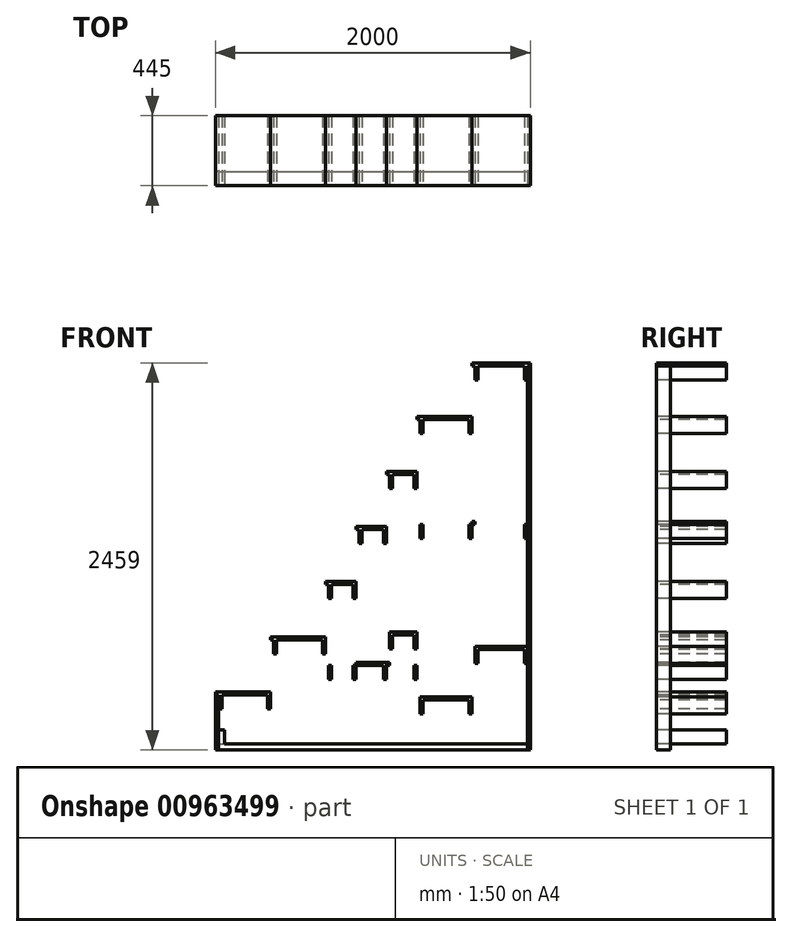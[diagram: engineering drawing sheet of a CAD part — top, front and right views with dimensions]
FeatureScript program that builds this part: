
annotation { "Feature Type Name" : "Feature", "Feature Type Description" : "" }
export const myFeature = defineFeature(function(context is Context, id is Id, definition is map)
    precondition{}
    {
        {
            var Q0;
            Q0=qCreatedBy(makeId("Front.planeOp"),FACE);
            var sketch = newSketch(context, id + "F0", { "sketchPlane" : qUnion([Q0])});
            skLineSegment(sketch, "E0.bottom", {"start": v(0, 0) * mm, "end": v(1962, 0) * mm});
            skLineSegment(sketch, "E0.top", {"start": v(0, 38) * mm, "end": v(1962, 38) * mm});
            skLineSegment(sketch, "E0.left", {"start": v(0, 0) * mm, "end": v(0, 38) * mm});
            skLineSegment(sketch, "E0.right", {"start": v(1962, 0) * mm, "end": v(1962, 38) * mm});
            skLineSegment(sketch, "E1.bottom", {"start": v(0, 0) * mm, "end": v(-19, 0) * mm});
            skLineSegment(sketch, "E1.top", {"start": v(0, 350) * mm, "end": v(-19, 350) * mm});
            skLineSegment(sketch, "E1.left", {"start": v(0, 0) * mm, "end": v(0, 350) * mm});
            skLineSegment(sketch, "E1.right", {"start": v(-19, 0) * mm, "end": v(-19, 350) * mm});
            skLineSegment(sketch, "E2.bottom", {"start": v(1962, 0) * mm, "end": v(1981, 0) * mm});
            skLineSegment(sketch, "E2.top", {"start": v(1962, 2440) * mm, "end": v(1981, 2440) * mm});
            skLineSegment(sketch, "E2.left", {"start": v(1962, 0) * mm, "end": v(1962, 2440) * mm});
            skLineSegment(sketch, "E2.right", {"start": v(1981, 0) * mm, "end": v(1981, 2440) * mm});
            skLineSegment(sketch, "E3.bottom", {"start": v(331, 38) * mm, "end": v(350, 38) * mm});
            skLineSegment(sketch, "E3.top", {"start": v(331, 700) * mm, "end": v(350, 700) * mm});
            skLineSegment(sketch, "E3.left", {"start": v(331, 38) * mm, "end": v(331, 700) * mm});
            skLineSegment(sketch, "E3.right", {"start": v(350, 38) * mm, "end": v(350, 700) * mm});
            skLineSegment(sketch, "E4.bottom", {"start": v(681, 38) * mm, "end": v(700, 38) * mm});
            skLineSegment(sketch, "E4.top", {"start": v(681, 1050) * mm, "end": v(700, 1050) * mm});
            skLineSegment(sketch, "E4.left", {"start": v(681, 38) * mm, "end": v(681, 1050) * mm});
            skLineSegment(sketch, "E4.right", {"start": v(700, 38) * mm, "end": v(700, 1050) * mm});
            skLineSegment(sketch, "E5.bottom", {"start": v(874.67, 38) * mm, "end": v(893.67, 38) * mm});
            skLineSegment(sketch, "E5.top", {"start": v(874.67, 1400) * mm, "end": v(893.67, 1400) * mm});
            skLineSegment(sketch, "E5.left", {"start": v(874.67, 38) * mm, "end": v(874.67, 1400) * mm});
            skLineSegment(sketch, "E5.right", {"start": v(893.67, 38) * mm, "end": v(893.67, 1400) * mm});
            skLineSegment(sketch, "E6.bottom", {"start": v(1068.34, 38) * mm, "end": v(1087.34, 38) * mm});
            skLineSegment(sketch, "E6.top", {"start": v(1068.34, 1750) * mm, "end": v(1087.34, 1750) * mm});
            skLineSegment(sketch, "E6.left", {"start": v(1068.34, 38) * mm, "end": v(1068.34, 1750) * mm});
            skLineSegment(sketch, "E6.right", {"start": v(1087.34, 38) * mm, "end": v(1087.34, 1750) * mm});
            skLineSegment(sketch, "E7.bottom", {"start": v(1262, 38) * mm, "end": v(1281, 38) * mm});
            skLineSegment(sketch, "E7.top", {"start": v(1262, 2100) * mm, "end": v(1281, 2100) * mm});
            skLineSegment(sketch, "E7.left", {"start": v(1262, 38) * mm, "end": v(1262, 2100) * mm});
            skLineSegment(sketch, "E7.right", {"start": v(1281, 38) * mm, "end": v(1281, 2100) * mm});
            skLineSegment(sketch, "E8.bottom", {"start": v(1612, 38) * mm, "end": v(1631, 38) * mm});
            skLineSegment(sketch, "E8.top", {"start": v(1612, 2440) * mm, "end": v(1631, 2440) * mm});
            skLineSegment(sketch, "E8.left", {"start": v(1612, 38) * mm, "end": v(1612, 2440) * mm});
            skLineSegment(sketch, "E8.right", {"start": v(1631, 38) * mm, "end": v(1631, 2440) * mm});
            skLineSegment(sketch, "E9", {"start": v(1612, 2440) * mm, "end": v(1962, 2440) * mm});
            skLineSegment(sketch, "E10", {"start": v(1281, 2100) * mm, "end": v(1612, 2100) * mm});
            skLineSegment(sketch, "E11", {"start": v(1087.34, 1750) * mm, "end": v(1262, 1750) * mm});
            skLineSegment(sketch, "E12", {"start": v(893.67, 1400) * mm, "end": v(1068.34, 1400) * mm});
            skLineSegment(sketch, "E13", {"start": v(700, 1050) * mm, "end": v(874.67, 1050) * mm});
            skLineSegment(sketch, "E14", {"start": v(350, 700) * mm, "end": v(681, 700) * mm});
            skLineSegment(sketch, "E15", {"start": v(0, 350) * mm, "end": v(331, 350) * mm});
            skLineSegment(sketch, "E16.bottom", {"start": v(0, 127) * mm, "end": v(38, 127) * mm});
            skLineSegment(sketch, "E16.top", {"start": v(0, 38) * mm, "end": v(38, 38) * mm});
            skLineSegment(sketch, "E16.left", {"start": v(0, 127) * mm, "end": v(0, 38) * mm});
            skLineSegment(sketch, "E16.right", {"start": v(38, 127) * mm, "end": v(38, 38) * mm});
            skLineSegment(sketch, "E17.bottom", {"start": v(0, 350) * mm, "end": v(22.52, 350) * mm});
            skLineSegment(sketch, "E17.top", {"start": v(0, 261) * mm, "end": v(22.52, 261) * mm});
            skLineSegment(sketch, "E17.left", {"start": v(0, 350) * mm, "end": v(0, 261) * mm});
            skLineSegment(sketch, "E17.right", {"start": v(22.52, 350) * mm, "end": v(22.52, 261) * mm});
            skLineSegment(sketch, "E18.bottom", {"start": v(312, 350) * mm, "end": v(331, 350) * mm});
            skLineSegment(sketch, "E18.top", {"start": v(312, 261) * mm, "end": v(331, 261) * mm});
            skLineSegment(sketch, "E18.left", {"start": v(312, 350) * mm, "end": v(312, 261) * mm});
            skLineSegment(sketch, "E18.right", {"start": v(331, 350) * mm, "end": v(331, 261) * mm});
            skLineSegment(sketch, "E19.bottom", {"start": v(-19, 350) * mm, "end": v(331, 350) * mm});
            skLineSegment(sketch, "E19.top", {"start": v(-19, 369) * mm, "end": v(331, 369) * mm});
            skLineSegment(sketch, "E19.left", {"start": v(-19, 350) * mm, "end": v(-19, 369) * mm});
            skLineSegment(sketch, "E19.right", {"start": v(331, 350) * mm, "end": v(331, 369) * mm});
            skLineSegment(sketch, "E20.bottom", {"start": v(350, 700) * mm, "end": v(369, 700) * mm});
            skLineSegment(sketch, "E20.top", {"start": v(350, 611) * mm, "end": v(369, 611) * mm});
            skLineSegment(sketch, "E20.left", {"start": v(350, 700) * mm, "end": v(350, 611) * mm});
            skLineSegment(sketch, "E20.right", {"start": v(369, 700) * mm, "end": v(369, 611) * mm});
            skLineSegment(sketch, "E21.bottom", {"start": v(681, 700) * mm, "end": v(662, 700) * mm});
            skLineSegment(sketch, "E21.top", {"start": v(681, 611) * mm, "end": v(662, 611) * mm});
            skLineSegment(sketch, "E21.left", {"start": v(681, 700) * mm, "end": v(681, 611) * mm});
            skLineSegment(sketch, "E21.right", {"start": v(662, 700) * mm, "end": v(662, 611) * mm});
            skLineSegment(sketch, "E22.bottom", {"start": v(331, 700) * mm, "end": v(681, 700) * mm});
            skLineSegment(sketch, "E22.top", {"start": v(331, 719) * mm, "end": v(681, 719) * mm});
            skLineSegment(sketch, "E22.left", {"start": v(331, 700) * mm, "end": v(331, 719) * mm});
            skLineSegment(sketch, "E22.right", {"start": v(681, 700) * mm, "end": v(681, 719) * mm});
            skLineSegment(sketch, "E23.bottom", {"start": v(700, 1050) * mm, "end": v(719, 1050) * mm});
            skLineSegment(sketch, "E23.top", {"start": v(700, 961) * mm, "end": v(719, 961) * mm});
            skLineSegment(sketch, "E23.left", {"start": v(700, 1050) * mm, "end": v(700, 961) * mm});
            skLineSegment(sketch, "E23.right", {"start": v(719, 1050) * mm, "end": v(719, 961) * mm});
            skLineSegment(sketch, "E24.bottom", {"start": v(874.67, 1050) * mm, "end": v(855.67, 1050) * mm});
            skLineSegment(sketch, "E24.top", {"start": v(874.67, 961) * mm, "end": v(855.67, 961) * mm});
            skLineSegment(sketch, "E24.left", {"start": v(874.67, 1050) * mm, "end": v(874.67, 961) * mm});
            skLineSegment(sketch, "E24.right", {"start": v(855.67, 1050) * mm, "end": v(855.67, 961) * mm});
            skLineSegment(sketch, "E25.bottom", {"start": v(681, 1050) * mm, "end": v(874.67, 1050) * mm});
            skLineSegment(sketch, "E25.top", {"start": v(681, 1069) * mm, "end": v(874.67, 1069) * mm});
            skLineSegment(sketch, "E25.left", {"start": v(681, 1050) * mm, "end": v(681, 1069) * mm});
            skLineSegment(sketch, "E25.right", {"start": v(874.67, 1050) * mm, "end": v(874.67, 1069) * mm});
            skLineSegment(sketch, "E26.bottom", {"start": v(893.67, 1400) * mm, "end": v(912.67, 1400) * mm});
            skLineSegment(sketch, "E26.top", {"start": v(893.67, 1311) * mm, "end": v(912.67, 1311) * mm});
            skLineSegment(sketch, "E26.left", {"start": v(893.67, 1400) * mm, "end": v(893.67, 1311) * mm});
            skLineSegment(sketch, "E26.right", {"start": v(912.67, 1400) * mm, "end": v(912.67, 1311) * mm});
            skLineSegment(sketch, "E27.bottom", {"start": v(1068.34, 1400) * mm, "end": v(1049.34, 1400) * mm});
            skLineSegment(sketch, "E27.top", {"start": v(1068.34, 1311) * mm, "end": v(1049.34, 1311) * mm});
            skLineSegment(sketch, "E27.left", {"start": v(1068.34, 1400) * mm, "end": v(1068.34, 1311) * mm});
            skLineSegment(sketch, "E27.right", {"start": v(1049.34, 1400) * mm, "end": v(1049.34, 1311) * mm});
            skLineSegment(sketch, "E28.bottom", {"start": v(874.67, 1400) * mm, "end": v(1068.34, 1400) * mm});
            skLineSegment(sketch, "E28.top", {"start": v(874.67, 1419) * mm, "end": v(1068.34, 1419) * mm});
            skLineSegment(sketch, "E28.left", {"start": v(874.67, 1400) * mm, "end": v(874.67, 1419) * mm});
            skLineSegment(sketch, "E28.right", {"start": v(1068.34, 1400) * mm, "end": v(1068.34, 1419) * mm});
            skLineSegment(sketch, "E29.bottom", {"start": v(1087.34, 1750) * mm, "end": v(1106.34, 1750) * mm});
            skLineSegment(sketch, "E29.top", {"start": v(1087.34, 1661) * mm, "end": v(1106.34, 1661) * mm});
            skLineSegment(sketch, "E29.left", {"start": v(1087.34, 1750) * mm, "end": v(1087.34, 1661) * mm});
            skLineSegment(sketch, "E29.right", {"start": v(1106.34, 1750) * mm, "end": v(1106.34, 1661) * mm});
            skLineSegment(sketch, "E30.bottom", {"start": v(1262, 1750) * mm, "end": v(1243, 1750) * mm});
            skLineSegment(sketch, "E30.top", {"start": v(1262, 1661) * mm, "end": v(1243, 1661) * mm});
            skLineSegment(sketch, "E30.left", {"start": v(1262, 1750) * mm, "end": v(1262, 1661) * mm});
            skLineSegment(sketch, "E30.right", {"start": v(1243, 1750) * mm, "end": v(1243, 1661) * mm});
            skLineSegment(sketch, "E31.bottom", {"start": v(1281, 2100) * mm, "end": v(1300, 2100) * mm});
            skLineSegment(sketch, "E31.top", {"start": v(1281, 2011) * mm, "end": v(1300, 2011) * mm});
            skLineSegment(sketch, "E31.left", {"start": v(1281, 2100) * mm, "end": v(1281, 2011) * mm});
            skLineSegment(sketch, "E31.right", {"start": v(1300, 2100) * mm, "end": v(1300, 2011) * mm});
            skLineSegment(sketch, "E32.bottom", {"start": v(1612, 2100) * mm, "end": v(1593, 2100) * mm});
            skLineSegment(sketch, "E32.top", {"start": v(1612, 2011) * mm, "end": v(1593, 2011) * mm});
            skLineSegment(sketch, "E32.left", {"start": v(1612, 2100) * mm, "end": v(1612, 2011) * mm});
            skLineSegment(sketch, "E32.right", {"start": v(1593, 2100) * mm, "end": v(1593, 2011) * mm});
            skLineSegment(sketch, "E33.bottom", {"start": v(1068.34, 1750) * mm, "end": v(1262, 1750) * mm});
            skLineSegment(sketch, "E33.top", {"start": v(1068.34, 1769) * mm, "end": v(1262, 1769) * mm});
            skLineSegment(sketch, "E33.left", {"start": v(1068.34, 1750) * mm, "end": v(1068.34, 1769) * mm});
            skLineSegment(sketch, "E33.right", {"start": v(1262, 1750) * mm, "end": v(1262, 1769) * mm});
            skLineSegment(sketch, "E34.bottom", {"start": v(1262, 2100) * mm, "end": v(1612, 2100) * mm});
            skLineSegment(sketch, "E34.top", {"start": v(1262, 2119) * mm, "end": v(1612, 2119) * mm});
            skLineSegment(sketch, "E34.left", {"start": v(1262, 2100) * mm, "end": v(1262, 2119) * mm});
            skLineSegment(sketch, "E34.right", {"start": v(1612, 2100) * mm, "end": v(1612, 2119) * mm});
            skLineSegment(sketch, "E35.bottom", {"start": v(1631, 2440) * mm, "end": v(1650, 2440) * mm});
            skLineSegment(sketch, "E35.top", {"start": v(1631, 2351) * mm, "end": v(1650, 2351) * mm});
            skLineSegment(sketch, "E35.left", {"start": v(1631, 2440) * mm, "end": v(1631, 2351) * mm});
            skLineSegment(sketch, "E35.right", {"start": v(1650, 2440) * mm, "end": v(1650, 2351) * mm});
            skLineSegment(sketch, "E36.bottom", {"start": v(1962, 2440) * mm, "end": v(1943, 2440) * mm});
            skLineSegment(sketch, "E36.top", {"start": v(1962, 2351) * mm, "end": v(1943, 2351) * mm});
            skLineSegment(sketch, "E36.left", {"start": v(1962, 2440) * mm, "end": v(1962, 2351) * mm});
            skLineSegment(sketch, "E36.right", {"start": v(1943, 2440) * mm, "end": v(1943, 2351) * mm});
            skLineSegment(sketch, "E37.bottom", {"start": v(1612, 2440) * mm, "end": v(1981, 2440) * mm});
            skLineSegment(sketch, "E37.top", {"start": v(1612, 2459) * mm, "end": v(1981, 2459) * mm});
            skLineSegment(sketch, "E37.left", {"start": v(1612, 2440) * mm, "end": v(1612, 2459) * mm});
            skLineSegment(sketch, "E37.right", {"start": v(1981, 2440) * mm, "end": v(1981, 2459) * mm});
            skLineSegment(sketch, "E38", {"start": v(1631, 638) * mm, "end": v(1962, 638) * mm});
            skLineSegment(sketch, "E39", {"start": v(1281, 319) * mm, "end": v(1612, 319) * mm});
            skLineSegment(sketch, "E40", {"start": v(1087.34, 731.7) * mm, "end": v(1262, 731.7) * mm});
            skLineSegment(sketch, "E41", {"start": v(1281, 1431.7) * mm, "end": v(1962, 1431.7) * mm});
            skLineSegment(sketch, "E42.bottom", {"start": v(1631, 638) * mm, "end": v(1650, 638) * mm});
            skLineSegment(sketch, "E42.top", {"start": v(1631, 549) * mm, "end": v(1650, 549) * mm});
            skLineSegment(sketch, "E42.left", {"start": v(1631, 638) * mm, "end": v(1631, 549) * mm});
            skLineSegment(sketch, "E42.right", {"start": v(1650, 638) * mm, "end": v(1650, 549) * mm});
            skLineSegment(sketch, "E43.bottom", {"start": v(1962, 638) * mm, "end": v(1943, 638) * mm});
            skLineSegment(sketch, "E43.top", {"start": v(1962, 549) * mm, "end": v(1943, 549) * mm});
            skLineSegment(sketch, "E43.left", {"start": v(1962, 638) * mm, "end": v(1962, 549) * mm});
            skLineSegment(sketch, "E43.right", {"start": v(1943, 638) * mm, "end": v(1943, 549) * mm});
            skLineSegment(sketch, "E44.bottom", {"start": v(1281, 319) * mm, "end": v(1300, 319) * mm});
            skLineSegment(sketch, "E44.top", {"start": v(1281, 230) * mm, "end": v(1300, 230) * mm});
            skLineSegment(sketch, "E44.left", {"start": v(1281, 319) * mm, "end": v(1281, 230) * mm});
            skLineSegment(sketch, "E44.right", {"start": v(1300, 319) * mm, "end": v(1300, 230) * mm});
            skLineSegment(sketch, "E45.bottom", {"start": v(1612, 319) * mm, "end": v(1593, 319) * mm});
            skLineSegment(sketch, "E45.top", {"start": v(1612, 230) * mm, "end": v(1593, 230) * mm});
            skLineSegment(sketch, "E45.left", {"start": v(1612, 319) * mm, "end": v(1612, 230) * mm});
            skLineSegment(sketch, "E45.right", {"start": v(1593, 319) * mm, "end": v(1593, 230) * mm});
            skLineSegment(sketch, "E46.bottom", {"start": v(1087.34, 731.7) * mm, "end": v(1106.34, 731.7) * mm});
            skLineSegment(sketch, "E46.top", {"start": v(1087.34, 642.7) * mm, "end": v(1106.34, 642.7) * mm});
            skLineSegment(sketch, "E46.left", {"start": v(1087.34, 731.7) * mm, "end": v(1087.34, 642.7) * mm});
            skLineSegment(sketch, "E46.right", {"start": v(1106.34, 731.7) * mm, "end": v(1106.34, 642.7) * mm});
            skLineSegment(sketch, "E47.bottom", {"start": v(1262, 731.7) * mm, "end": v(1243, 731.7) * mm});
            skLineSegment(sketch, "E47.top", {"start": v(1262, 642.7) * mm, "end": v(1243, 642.7) * mm});
            skLineSegment(sketch, "E47.left", {"start": v(1262, 731.7) * mm, "end": v(1262, 642.7) * mm});
            skLineSegment(sketch, "E47.right", {"start": v(1243, 731.7) * mm, "end": v(1243, 642.7) * mm});
            skLineSegment(sketch, "E48.bottom", {"start": v(1281, 1431.7) * mm, "end": v(1300, 1431.7) * mm});
            skLineSegment(sketch, "E48.top", {"start": v(1281, 1342.7) * mm, "end": v(1300, 1342.7) * mm});
            skLineSegment(sketch, "E48.left", {"start": v(1281, 1431.7) * mm, "end": v(1281, 1342.7) * mm});
            skLineSegment(sketch, "E48.right", {"start": v(1300, 1431.7) * mm, "end": v(1300, 1342.7) * mm});
            skLineSegment(sketch, "E49.bottom", {"start": v(1612, 1431.7) * mm, "end": v(1593, 1431.7) * mm});
            skLineSegment(sketch, "E49.top", {"start": v(1612, 1342.7) * mm, "end": v(1593, 1342.7) * mm});
            skLineSegment(sketch, "E49.left", {"start": v(1612, 1431.7) * mm, "end": v(1612, 1342.7) * mm});
            skLineSegment(sketch, "E49.right", {"start": v(1593, 1431.7) * mm, "end": v(1593, 1342.7) * mm});
            skLineSegment(sketch, "E50.bottom", {"start": v(1962, 1431.7) * mm, "end": v(1943, 1431.7) * mm});
            skLineSegment(sketch, "E50.top", {"start": v(1962, 1342.7) * mm, "end": v(1943, 1342.7) * mm});
            skLineSegment(sketch, "E50.left", {"start": v(1962, 1431.7) * mm, "end": v(1962, 1342.7) * mm});
            skLineSegment(sketch, "E50.right", {"start": v(1943, 1431.7) * mm, "end": v(1943, 1342.7) * mm});
            skLineSegment(sketch, "E51.top", {"start": v(1631, 657) * mm, "end": v(1962, 657) * mm});
            skLineSegment(sketch, "E51.left", {"start": v(1631, 638) * mm, "end": v(1631, 657) * mm});
            skLineSegment(sketch, "E51.right", {"start": v(1962, 638) * mm, "end": v(1962, 657) * mm});
            skLineSegment(sketch, "E52.top", {"start": v(1281, 338) * mm, "end": v(1612, 338) * mm});
            skLineSegment(sketch, "E52.left", {"start": v(1281, 319) * mm, "end": v(1281, 338) * mm});
            skLineSegment(sketch, "E52.right", {"start": v(1612, 319) * mm, "end": v(1612, 338) * mm});
            skLineSegment(sketch, "E53.top", {"start": v(1087.34, 750.7) * mm, "end": v(1262, 750.7) * mm});
            skLineSegment(sketch, "E53.left", {"start": v(1087.34, 731.7) * mm, "end": v(1087.34, 750.7) * mm});
            skLineSegment(sketch, "E53.right", {"start": v(1262, 731.7) * mm, "end": v(1262, 750.7) * mm});
            skLineSegment(sketch, "E54.top", {"start": v(1281, 1450.7) * mm, "end": v(1962, 1450.7) * mm});
            skLineSegment(sketch, "E54.left", {"start": v(1281, 1431.7) * mm, "end": v(1281, 1450.7) * mm});
            skLineSegment(sketch, "E54.right", {"start": v(1962, 1431.7) * mm, "end": v(1962, 1450.7) * mm});
            skLineSegment(sketch, "E55.bottom", {"start": v(700, 538) * mm, "end": v(719, 538) * mm});
            skLineSegment(sketch, "E55.top", {"start": v(700, 449) * mm, "end": v(719, 449) * mm});
            skLineSegment(sketch, "E55.left", {"start": v(700, 538) * mm, "end": v(700, 449) * mm});
            skLineSegment(sketch, "E55.right", {"start": v(719, 538) * mm, "end": v(719, 449) * mm});
            skLineSegment(sketch, "E56.bottom", {"start": v(874.3, 538) * mm, "end": v(855.3, 538) * mm});
            skLineSegment(sketch, "E56.top", {"start": v(874.3, 449) * mm, "end": v(855.3, 449) * mm});
            skLineSegment(sketch, "E56.left", {"start": v(874.3, 538) * mm, "end": v(874.3, 449) * mm});
            skLineSegment(sketch, "E56.right", {"start": v(855.3, 538) * mm, "end": v(855.3, 449) * mm});
            skLineSegment(sketch, "E57.bottom", {"start": v(1068.34, 538) * mm, "end": v(1049.34, 538) * mm});
            skLineSegment(sketch, "E57.top", {"start": v(1068.34, 449) * mm, "end": v(1049.34, 449) * mm});
            skLineSegment(sketch, "E57.left", {"start": v(1068.34, 538) * mm, "end": v(1068.34, 449) * mm});
            skLineSegment(sketch, "E57.right", {"start": v(1049.34, 538) * mm, "end": v(1049.34, 449) * mm});
            skLineSegment(sketch, "E58.bottom", {"start": v(1262, 538) * mm, "end": v(1243, 538) * mm});
            skLineSegment(sketch, "E58.top", {"start": v(1262, 449) * mm, "end": v(1243, 449) * mm});
            skLineSegment(sketch, "E58.left", {"start": v(1262, 538) * mm, "end": v(1262, 449) * mm});
            skLineSegment(sketch, "E58.right", {"start": v(1243, 538) * mm, "end": v(1243, 449) * mm});
            skLineSegment(sketch, "E59.bottom", {"start": v(700, 538) * mm, "end": v(1262, 538) * mm});
            skLineSegment(sketch, "E59.top", {"start": v(700, 557) * mm, "end": v(1262, 557) * mm});
            skLineSegment(sketch, "E59.left", {"start": v(700, 538) * mm, "end": v(700, 557) * mm});
            skLineSegment(sketch, "E59.right", {"start": v(1262, 538) * mm, "end": v(1262, 557) * mm});
            skLineSegment(sketch, "E60.bottom", {"start": v(350, 38) * mm, "end": v(388, 38) * mm});
            skLineSegment(sketch, "E60.top", {"start": v(350, 127) * mm, "end": v(388, 127) * mm});
            skLineSegment(sketch, "E60.left", {"start": v(350, 38) * mm, "end": v(350, 127) * mm});
            skLineSegment(sketch, "E60.right", {"start": v(388, 38) * mm, "end": v(388, 127) * mm});
            skLineSegment(sketch, "E61.bottom", {"start": v(700, 38) * mm, "end": v(738, 38) * mm});
            skLineSegment(sketch, "E61.top", {"start": v(700, 127) * mm, "end": v(738, 127) * mm});
            skLineSegment(sketch, "E61.left", {"start": v(700, 38) * mm, "end": v(700, 127) * mm});
            skLineSegment(sketch, "E61.right", {"start": v(738, 38) * mm, "end": v(738, 127) * mm});
            skLineSegment(sketch, "E62.bottom", {"start": v(893.67, 38) * mm, "end": v(931.67, 38) * mm});
            skLineSegment(sketch, "E62.top", {"start": v(893.67, 127) * mm, "end": v(931.67, 127) * mm});
            skLineSegment(sketch, "E62.left", {"start": v(893.67, 38) * mm, "end": v(893.67, 127) * mm});
            skLineSegment(sketch, "E62.right", {"start": v(931.67, 38) * mm, "end": v(931.67, 127) * mm});
            skLineSegment(sketch, "E63.bottom", {"start": v(1087.34, 38) * mm, "end": v(1125.34, 38) * mm});
            skLineSegment(sketch, "E63.top", {"start": v(1087.34, 127) * mm, "end": v(1125.34, 127) * mm});
            skLineSegment(sketch, "E63.left", {"start": v(1087.34, 38) * mm, "end": v(1087.34, 127) * mm});
            skLineSegment(sketch, "E63.right", {"start": v(1125.34, 38) * mm, "end": v(1125.34, 127) * mm});
            skLineSegment(sketch, "E64.bottom", {"start": v(1281, 38) * mm, "end": v(1319, 38) * mm});
            skLineSegment(sketch, "E64.top", {"start": v(1281, 127) * mm, "end": v(1319, 127) * mm});
            skLineSegment(sketch, "E64.left", {"start": v(1281, 38) * mm, "end": v(1281, 127) * mm});
            skLineSegment(sketch, "E64.right", {"start": v(1319, 38) * mm, "end": v(1319, 127) * mm});
            skLineSegment(sketch, "E65.bottom", {"start": v(1631, 38) * mm, "end": v(1669, 38) * mm});
            skLineSegment(sketch, "E65.top", {"start": v(1631, 127) * mm, "end": v(1669, 127) * mm});
            skLineSegment(sketch, "E65.left", {"start": v(1631, 38) * mm, "end": v(1631, 127) * mm});
            skLineSegment(sketch, "E65.right", {"start": v(1669, 38) * mm, "end": v(1669, 127) * mm});
            skLineSegment(sketch, "E66.bottom", {"start": v(1962, 38) * mm, "end": v(1924, 38) * mm});
            skLineSegment(sketch, "E66.top", {"start": v(1962, 127) * mm, "end": v(1924, 127) * mm});
            skLineSegment(sketch, "E66.left", {"start": v(1962, 38) * mm, "end": v(1962, 127) * mm});
            skLineSegment(sketch, "E66.right", {"start": v(1924, 38) * mm, "end": v(1924, 127) * mm});
            skSolve(sketch);
        }
        {
            var Q0;
            {var subQ12=sQuery(id+"F0.wireOp",EDGE,"E0.bottom");Q0=makeQuery(id+"F0.imprint","IMPRINT",FACE,{"disambiguationData":[TD([[makeQuery(id+"F0.imprint","IMPRINT",EDGE,{"derivedFrom":subQ12}),1.0]])]});}
            extrude(context, id + "F1", {"entities" : qUnion([Q0]), "oppositeDirection" : true, "depth" : 89 * mm, "offsetDistance" : 25 * mm});
        }
        {
            var Q0;
            Q0=makeQuery(id+"F0.imprint","IMPRINT",FACE,{"disambiguationData":[TD([[makeQuery(id+"F0.imprint","IMPRINT",EDGE,{"derivedFrom":sQuery(id+"F0.wireOp",EDGE,"E16.bottom")}),-1.0]])]});
            var Q1;
            Q1=makeQuery(id+"F0.imprint","IMPRINT",FACE,{"disambiguationData":[TD([[makeQuery(id+"F0.imprint","IMPRINT",EDGE,{"derivedFrom":sQuery(id+"F0.wireOp",EDGE,"E60.bottom")}),1.0]])]});
            var Q2;
            Q2=makeQuery(id+"F0.imprint","IMPRINT",FACE,{"disambiguationData":[TD([[makeQuery(id+"F0.imprint","IMPRINT",EDGE,{"derivedFrom":sQuery(id+"F0.wireOp",EDGE,"E61.bottom")}),1.0]])]});
            var Q3;
            Q3=makeQuery(id+"F0.imprint","IMPRINT",FACE,{"disambiguationData":[TD([[makeQuery(id+"F0.imprint","IMPRINT",EDGE,{"derivedFrom":sQuery(id+"F0.wireOp",EDGE,"E62.bottom")}),1.0]])]});
            var Q4;
            Q4=makeQuery(id+"F0.imprint","IMPRINT",FACE,{"disambiguationData":[TD([[makeQuery(id+"F0.imprint","IMPRINT",EDGE,{"derivedFrom":sQuery(id+"F0.wireOp",EDGE,"E63.bottom")}),1.0]])]});
            var Q5;
            Q5=makeQuery(id+"F0.imprint","IMPRINT",FACE,{"disambiguationData":[TD([[makeQuery(id+"F0.imprint","IMPRINT",EDGE,{"derivedFrom":sQuery(id+"F0.wireOp",EDGE,"E64.bottom")}),1.0]])]});
            var Q6;
            Q6=makeQuery(id+"F0.imprint","IMPRINT",FACE,{"disambiguationData":[TD([[makeQuery(id+"F0.imprint","IMPRINT",EDGE,{"derivedFrom":sQuery(id+"F0.wireOp",EDGE,"E65.bottom")}),1.0]])]});
            var Q7;
            Q7=makeQuery(id+"F0.imprint","IMPRINT",FACE,{"disambiguationData":[TD([[makeQuery(id+"F0.imprint","IMPRINT",EDGE,{"derivedFrom":sQuery(id+"F0.wireOp",EDGE,"E66.bottom")}),-1.0]])]});
            var Q8;
            Q8=makeQuery(id+"F0.imprint","IMPRINT",FACE,{"disambiguationData":[TD([[makeQuery(id+"F0.imprint","IMPRINT",EDGE,{"derivedFrom":sQuery(id+"F0.wireOp",EDGE,"E45.top")}),-1.0]])]});
            var Q9;
            Q9=makeQuery(id+"F0.imprint","IMPRINT",FACE,{"disambiguationData":[TD([[makeQuery(id+"F0.imprint","IMPRINT",EDGE,{"derivedFrom":sQuery(id+"F0.wireOp",EDGE,"E44.top")}),1.0]])]});
            var Q10;
            Q10=makeQuery(id+"F0.imprint","IMPRINT",FACE,{"disambiguationData":[TD([[makeQuery(id+"F0.imprint","IMPRINT",EDGE,{"derivedFrom":sQuery(id+"F0.wireOp",EDGE,"E58.top")}),-1.0]])]});
            var Q11;
            Q11=makeQuery(id+"F0.imprint","IMPRINT",FACE,{"disambiguationData":[TD([[makeQuery(id+"F0.imprint","IMPRINT",EDGE,{"derivedFrom":sQuery(id+"F0.wireOp",EDGE,"E57.top")}),-1.0]])]});
            var Q12;
            Q12=makeQuery(id+"F0.imprint","IMPRINT",FACE,{"disambiguationData":[TD([[makeQuery(id+"F0.imprint","IMPRINT",EDGE,{"derivedFrom":sQuery(id+"F0.wireOp",EDGE,"E56.top")}),-1.0]])]});
            var Q13;
            Q13=makeQuery(id+"F0.imprint","IMPRINT",FACE,{"disambiguationData":[TD([[makeQuery(id+"F0.imprint","IMPRINT",EDGE,{"derivedFrom":sQuery(id+"F0.wireOp",EDGE,"E55.top")}),1.0]])]});
            var Q14;
            Q14=makeQuery(id+"F0.imprint","IMPRINT",FACE,{"disambiguationData":[TD([[makeQuery(id+"F0.imprint","IMPRINT",EDGE,{"derivedFrom":sQuery(id+"F0.wireOp",EDGE,"E18.top")}),1.0]])]});
            var Q15;
            Q15=makeQuery(id+"F0.imprint","IMPRINT",FACE,{"disambiguationData":[TD([[makeQuery(id+"F0.imprint","IMPRINT",EDGE,{"derivedFrom":sQuery(id+"F0.wireOp",EDGE,"E17.top")}),1.0]])]});
            var Q16;
            Q16=makeQuery(id+"F0.imprint","IMPRINT",FACE,{"disambiguationData":[TD([[makeQuery(id+"F0.imprint","IMPRINT",EDGE,{"derivedFrom":sQuery(id+"F0.wireOp",EDGE,"E20.top")}),1.0]])]});
            var Q17;
            Q17=makeQuery(id+"F0.imprint","IMPRINT",FACE,{"disambiguationData":[TD([[makeQuery(id+"F0.imprint","IMPRINT",EDGE,{"derivedFrom":sQuery(id+"F0.wireOp",EDGE,"E21.top")}),-1.0]])]});
            var Q18;
            Q18=makeQuery(id+"F0.imprint","IMPRINT",FACE,{"disambiguationData":[TD([[makeQuery(id+"F0.imprint","IMPRINT",EDGE,{"derivedFrom":sQuery(id+"F0.wireOp",EDGE,"E46.top")}),1.0]])]});
            var Q19;
            Q19=makeQuery(id+"F0.imprint","IMPRINT",FACE,{"disambiguationData":[TD([[makeQuery(id+"F0.imprint","IMPRINT",EDGE,{"derivedFrom":sQuery(id+"F0.wireOp",EDGE,"E47.top")}),-1.0]])]});
            var Q20;
            Q20=makeQuery(id+"F0.imprint","IMPRINT",FACE,{"disambiguationData":[TD([[makeQuery(id+"F0.imprint","IMPRINT",EDGE,{"derivedFrom":sQuery(id+"F0.wireOp",EDGE,"E42.top")}),1.0]])]});
            var Q21;
            Q21=makeQuery(id+"F0.imprint","IMPRINT",FACE,{"disambiguationData":[TD([[makeQuery(id+"F0.imprint","IMPRINT",EDGE,{"derivedFrom":sQuery(id+"F0.wireOp",EDGE,"E43.top")}),-1.0]])]});
            var Q22;
            Q22=makeQuery(id+"F0.imprint","IMPRINT",FACE,{"disambiguationData":[TD([[makeQuery(id+"F0.imprint","IMPRINT",EDGE,{"derivedFrom":sQuery(id+"F0.wireOp",EDGE,"E23.top")}),1.0]])]});
            var Q23;
            Q23=makeQuery(id+"F0.imprint","IMPRINT",FACE,{"disambiguationData":[TD([[makeQuery(id+"F0.imprint","IMPRINT",EDGE,{"derivedFrom":sQuery(id+"F0.wireOp",EDGE,"E24.top")}),-1.0]])]});
            var Q24;
            Q24=makeQuery(id+"F0.imprint","IMPRINT",FACE,{"disambiguationData":[TD([[makeQuery(id+"F0.imprint","IMPRINT",EDGE,{"derivedFrom":sQuery(id+"F0.wireOp",EDGE,"E26.top")}),1.0]])]});
            var Q25;
            Q25=makeQuery(id+"F0.imprint","IMPRINT",FACE,{"disambiguationData":[TD([[makeQuery(id+"F0.imprint","IMPRINT",EDGE,{"derivedFrom":sQuery(id+"F0.wireOp",EDGE,"E27.top")}),-1.0]])]});
            var Q26;
            Q26=makeQuery(id+"F0.imprint","IMPRINT",FACE,{"disambiguationData":[TD([[makeQuery(id+"F0.imprint","IMPRINT",EDGE,{"derivedFrom":sQuery(id+"F0.wireOp",EDGE,"E48.top")}),1.0]])]});
            var Q27;
            Q27=makeQuery(id+"F0.imprint","IMPRINT",FACE,{"disambiguationData":[TD([[makeQuery(id+"F0.imprint","IMPRINT",EDGE,{"derivedFrom":sQuery(id+"F0.wireOp",EDGE,"E49.top")}),-1.0]])]});
            var Q28;
            Q28=makeQuery(id+"F0.imprint","IMPRINT",FACE,{"disambiguationData":[TD([[makeQuery(id+"F0.imprint","IMPRINT",EDGE,{"derivedFrom":sQuery(id+"F0.wireOp",EDGE,"E50.top")}),-1.0]])]});
            var Q29;
            Q29=makeQuery(id+"F0.imprint","IMPRINT",FACE,{"disambiguationData":[TD([[makeQuery(id+"F0.imprint","IMPRINT",EDGE,{"derivedFrom":sQuery(id+"F0.wireOp",EDGE,"E29.top")}),1.0]])]});
            var Q30;
            Q30=makeQuery(id+"F0.imprint","IMPRINT",FACE,{"disambiguationData":[TD([[makeQuery(id+"F0.imprint","IMPRINT",EDGE,{"derivedFrom":sQuery(id+"F0.wireOp",EDGE,"E30.top")}),-1.0]])]});
            var Q31;
            Q31=makeQuery(id+"F0.imprint","IMPRINT",FACE,{"disambiguationData":[TD([[makeQuery(id+"F0.imprint","IMPRINT",EDGE,{"derivedFrom":sQuery(id+"F0.wireOp",EDGE,"E31.top")}),1.0]])]});
            var Q32;
            Q32=makeQuery(id+"F0.imprint","IMPRINT",FACE,{"disambiguationData":[TD([[makeQuery(id+"F0.imprint","IMPRINT",EDGE,{"derivedFrom":sQuery(id+"F0.wireOp",EDGE,"E32.top")}),-1.0]])]});
            var Q33;
            Q33=makeQuery(id+"F0.imprint","IMPRINT",FACE,{"disambiguationData":[TD([[makeQuery(id+"F0.imprint","IMPRINT",EDGE,{"derivedFrom":sQuery(id+"F0.wireOp",EDGE,"E35.top")}),1.0]])]});
            var Q34;
            Q34=makeQuery(id+"F0.imprint","IMPRINT",FACE,{"disambiguationData":[TD([[makeQuery(id+"F0.imprint","IMPRINT",EDGE,{"derivedFrom":sQuery(id+"F0.wireOp",EDGE,"E36.top")}),-1.0]])]});
            var Q35;
            Q35=makeQuery(id+"F0.imprint","IMPRINT",FACE,{"disambiguationData":[TD([[makeQuery(id+"F0.imprint","IMPRINT",EDGE,{"derivedFrom":sQuery(id+"F0.wireOp",EDGE,"E19.top")}),-1.0]])]});
            var Q36;
            Q36=makeQuery(id+"F0.imprint","IMPRINT",FACE,{"disambiguationData":[TD([[makeQuery(id+"F0.imprint","IMPRINT",EDGE,{"derivedFrom":sQuery(id+"F0.wireOp",EDGE,"E22.top")}),-1.0]])]});
            var Q37;
            Q37=makeQuery(id+"F0.imprint","IMPRINT",FACE,{"disambiguationData":[TD([[makeQuery(id+"F0.imprint","IMPRINT",EDGE,{"derivedFrom":sQuery(id+"F0.wireOp",EDGE,"E25.top")}),-1.0]])]});
            var Q38;
            Q38=makeQuery(id+"F0.imprint","IMPRINT",FACE,{"disambiguationData":[TD([[makeQuery(id+"F0.imprint","IMPRINT",EDGE,{"derivedFrom":sQuery(id+"F0.wireOp",EDGE,"E28.top")}),-1.0]])]});
            var Q39;
            Q39=makeQuery(id+"F0.imprint","IMPRINT",FACE,{"disambiguationData":[TD([[makeQuery(id+"F0.imprint","IMPRINT",EDGE,{"derivedFrom":sQuery(id+"F0.wireOp",EDGE,"E53.top")}),-1.0]])]});
            var Q40;
            {var subQ0=sQuery(id+"F0.wireOp",EDGE,"E59.right");Q40=makeQuery(id+"F0.imprint","IMPRINT",FACE,{"disambiguationData":[TD([[makeQuery(id+"F0.imprint","IMPRINT",EDGE,{"derivedFrom":subQ0}),1.0]])]});}
            var Q41;
            {var subQ0=sQuery(id+"F0.wireOp",EDGE,"E59.bottom");var subQ5=sQuery(id+"F0.wireOp",EDGE,"E6.right");var subQ6=makeQuery(id+"F0.imprint","INTERSECT",VERTEX,{"derivedFrom":[subQ5,subQ0]});Q41=makeQuery(id+"F0.imprint","IMPRINT",FACE,{"disambiguationData":[TD([[makeQuery(id+"F0.imprint","IMPRINT",EDGE,{"disambiguationData":[TD([[subQ6,-1.0]])],"derivedFrom":subQ5}),1.0]])]});}
            var Q42;
            {var subQ0=sQuery(id+"F0.wireOp",EDGE,"E59.bottom");var subQ2=sQuery(id+"F0.wireOp",EDGE,"E5.right");var subQ3=makeQuery(id+"F0.imprint","INTERSECT",VERTEX,{"derivedFrom":[subQ2,subQ0]});Q42=makeQuery(id+"F0.imprint","IMPRINT",FACE,{"disambiguationData":[TD([[makeQuery(id+"F0.imprint","IMPRINT",EDGE,{"disambiguationData":[TD([[subQ3,-1.0]])],"derivedFrom":subQ2}),-1.0]])]});}
            var Q43;
            {var subQ0=sQuery(id+"F0.wireOp",EDGE,"E59.bottom");var subQ1=sQuery(id+"F0.wireOp",EDGE,"E5.left");var subQ2=makeQuery(id+"F0.imprint","INTERSECT",VERTEX,{"derivedFrom":[subQ1,subQ0]});Q43=makeQuery(id+"F0.imprint","IMPRINT",FACE,{"disambiguationData":[TD([[makeQuery(id+"F0.imprint","IMPRINT",EDGE,{"disambiguationData":[TD([[subQ2,-1.0]])],"derivedFrom":subQ1}),-1.0]])]});}
            var Q44;
            {var subQ8=sQuery(id+"F0.wireOp",EDGE,"E59.left");Q44=makeQuery(id+"F0.imprint","IMPRINT",FACE,{"disambiguationData":[TD([[makeQuery(id+"F0.imprint","IMPRINT",EDGE,{"derivedFrom":subQ8}),-1.0]])]});}
            var Q45;
            Q45=makeQuery(id+"F0.imprint","IMPRINT",FACE,{"disambiguationData":[TD([[makeQuery(id+"F0.imprint","IMPRINT",EDGE,{"derivedFrom":sQuery(id+"F0.wireOp",EDGE,"E52.top")}),-1.0]])]});
            var Q46;
            Q46=makeQuery(id+"F0.imprint","IMPRINT",FACE,{"disambiguationData":[TD([[makeQuery(id+"F0.imprint","IMPRINT",EDGE,{"derivedFrom":sQuery(id+"F0.wireOp",EDGE,"E51.top")}),-1.0]])]});
            var Q47;
            {var subQ3=sQuery(id+"F0.wireOp",EDGE,"E54.left");Q47=makeQuery(id+"F0.imprint","IMPRINT",FACE,{"disambiguationData":[TD([[makeQuery(id+"F0.imprint","IMPRINT",EDGE,{"derivedFrom":subQ3}),-1.0]])]});}
            var Q48;
            {var subQ0=sQuery(id+"F0.wireOp",EDGE,"E41");var subQ5=sQuery(id+"F0.wireOp",EDGE,"E8.right");var subQ6=makeQuery(id+"F0.imprint","INTERSECT",VERTEX,{"derivedFrom":[subQ5,subQ0]});Q48=makeQuery(id+"F0.imprint","IMPRINT",FACE,{"disambiguationData":[TD([[makeQuery(id+"F0.imprint","IMPRINT",EDGE,{"disambiguationData":[TD([[subQ6,-1.0]])],"derivedFrom":subQ5}),1.0]])]});}
            var Q49;
            {var subQ0=sQuery(id+"F0.wireOp",EDGE,"E54.right");Q49=makeQuery(id+"F0.imprint","IMPRINT",FACE,{"disambiguationData":[TD([[makeQuery(id+"F0.imprint","IMPRINT",EDGE,{"derivedFrom":subQ0}),1.0]])]});}
            var Q50;
            Q50=makeQuery(id+"F0.imprint","IMPRINT",FACE,{"disambiguationData":[TD([[makeQuery(id+"F0.imprint","IMPRINT",EDGE,{"derivedFrom":sQuery(id+"F0.wireOp",EDGE,"E33.top")}),-1.0]])]});
            var Q51;
            Q51=makeQuery(id+"F0.imprint","IMPRINT",FACE,{"disambiguationData":[TD([[makeQuery(id+"F0.imprint","IMPRINT",EDGE,{"derivedFrom":sQuery(id+"F0.wireOp",EDGE,"E34.top")}),-1.0]])]});
            var Q52;
            Q52=makeQuery(id+"F0.imprint","IMPRINT",FACE,{"disambiguationData":[TD([[makeQuery(id+"F0.imprint","IMPRINT",EDGE,{"derivedFrom":sQuery(id+"F0.wireOp",EDGE,"E37.top")}),-1.0]])]});
            extrude(context, id + "F2", {"entities" : qUnion([Q0, Q1, Q2, Q3, Q4, Q5, Q6, Q7, Q8, Q9, Q10, Q11, Q12, Q13, Q14, Q15, Q16, Q17, Q18, Q19, Q20, Q21, Q22, Q23, Q24, Q25, Q26, Q27, Q28, Q29, Q30, Q31, Q32, Q33, Q34, Q35, Q36, Q37, Q38, Q39, Q40, Q41, Q42, Q43, Q44, Q45, Q46, Q47, Q48, Q49, Q50, Q51, Q52]), "operationType" : NewBodyOperationType.ADD, "oppositeDirection" : true, "depth" : 445 * mm, "offsetDistance" : 25 * mm});
        }
        {
            var Q0;
            {var subQ8=sQuery(id+"F0.wireOp",EDGE,"E2.bottom");Q0=makeQuery(id+"F0.imprint","IMPRINT",FACE,{"disambiguationData":[TD([[makeQuery(id+"F0.imprint","IMPRINT",EDGE,{"derivedFrom":subQ8}),1.0]])]});}
            var Q1;
            {var subQ4=sQuery(id+"F0.wireOp",EDGE,"E1.bottom");Q1=makeQuery(id+"F0.imprint","IMPRINT",FACE,{"disambiguationData":[TD([[makeQuery(id+"F0.imprint","IMPRINT",EDGE,{"derivedFrom":subQ4}),-1.0]])]});}
            var Q2;
            {var subQ4=sQuery(id+"F0.wireOp",EDGE,"E3.bottom");Q2=makeQuery(id+"F0.imprint","IMPRINT",FACE,{"disambiguationData":[TD([[makeQuery(id+"F0.imprint","IMPRINT",EDGE,{"derivedFrom":subQ4}),1.0]])]});}
            var Q3;
            {var subQ9=sQuery(id+"F0.wireOp",EDGE,"E4.bottom");Q3=makeQuery(id+"F0.imprint","IMPRINT",FACE,{"disambiguationData":[TD([[makeQuery(id+"F0.imprint","IMPRINT",EDGE,{"derivedFrom":subQ9}),1.0]])]});}
            var Q4;
            {var subQ6=sQuery(id+"F0.wireOp",EDGE,"E5.bottom");Q4=makeQuery(id+"F0.imprint","IMPRINT",FACE,{"disambiguationData":[TD([[makeQuery(id+"F0.imprint","IMPRINT",EDGE,{"derivedFrom":subQ6}),1.0]])]});}
            var Q5;
            {var subQ7=sQuery(id+"F0.wireOp",EDGE,"E24.left");Q5=makeQuery(id+"F0.imprint","IMPRINT",FACE,{"disambiguationData":[TD([[makeQuery(id+"F0.imprint","IMPRINT",EDGE,{"derivedFrom":subQ7}),1.0]])]});}
            var Q6;
            {var subQ0=sQuery(id+"F0.wireOp",EDGE,"E59.bottom");var subQ1=sQuery(id+"F0.wireOp",EDGE,"E5.left");var subQ2=makeQuery(id+"F0.imprint","INTERSECT",VERTEX,{"derivedFrom":[subQ1,subQ0]});Q6=makeQuery(id+"F0.imprint","IMPRINT",FACE,{"disambiguationData":[TD([[makeQuery(id+"F0.imprint","IMPRINT",EDGE,{"disambiguationData":[TD([[subQ2,-1.0]])],"derivedFrom":subQ1}),-1.0]])]});}
            var Q7;
            {var subQ2=sQuery(id+"F0.wireOp",EDGE,"E6.bottom");Q7=makeQuery(id+"F0.imprint","IMPRINT",FACE,{"disambiguationData":[TD([[makeQuery(id+"F0.imprint","IMPRINT",EDGE,{"derivedFrom":subQ2}),1.0]])]});}
            var Q8;
            {var subQ0=sQuery(id+"F0.wireOp",EDGE,"E59.bottom");var subQ5=sQuery(id+"F0.wireOp",EDGE,"E6.right");var subQ6=makeQuery(id+"F0.imprint","INTERSECT",VERTEX,{"derivedFrom":[subQ5,subQ0]});Q8=makeQuery(id+"F0.imprint","IMPRINT",FACE,{"disambiguationData":[TD([[makeQuery(id+"F0.imprint","IMPRINT",EDGE,{"disambiguationData":[TD([[subQ6,-1.0]])],"derivedFrom":subQ5}),1.0]])]});}
            var Q9;
            {var subQ1=sQuery(id+"F0.wireOp",EDGE,"E27.left");Q9=makeQuery(id+"F0.imprint","IMPRINT",FACE,{"disambiguationData":[TD([[makeQuery(id+"F0.imprint","IMPRINT",EDGE,{"derivedFrom":subQ1}),1.0]])]});}
            var Q10;
            {var subQ11=sQuery(id+"F0.wireOp",EDGE,"E7.bottom");Q10=makeQuery(id+"F0.imprint","IMPRINT",FACE,{"disambiguationData":[TD([[makeQuery(id+"F0.imprint","IMPRINT",EDGE,{"derivedFrom":subQ11}),1.0]])]});}
            var Q11;
            {var subQ6=sQuery(id+"F0.wireOp",EDGE,"E8.bottom");Q11=makeQuery(id+"F0.imprint","IMPRINT",FACE,{"disambiguationData":[TD([[makeQuery(id+"F0.imprint","IMPRINT",EDGE,{"derivedFrom":subQ6}),1.0]])]});}
            var Q12;
            {var subQ0=sQuery(id+"F0.wireOp",EDGE,"E41");var subQ5=sQuery(id+"F0.wireOp",EDGE,"E8.right");var subQ6=makeQuery(id+"F0.imprint","INTERSECT",VERTEX,{"derivedFrom":[subQ5,subQ0]});Q12=makeQuery(id+"F0.imprint","IMPRINT",FACE,{"disambiguationData":[TD([[makeQuery(id+"F0.imprint","IMPRINT",EDGE,{"disambiguationData":[TD([[subQ6,-1.0]])],"derivedFrom":subQ5}),1.0]])]});}
            var Q13;
            {var subQ0=sQuery(id+"F0.wireOp",EDGE,"E32.left");Q13=makeQuery(id+"F0.imprint","IMPRINT",FACE,{"disambiguationData":[TD([[makeQuery(id+"F0.imprint","IMPRINT",EDGE,{"derivedFrom":subQ0}),1.0]])]});}
            extrude(context, id + "F3", {"entities" : qUnion([Q0, Q1, Q2, Q3, Q4, Q5, Q6, Q7, Q8, Q9, Q10, Q11, Q12, Q13]), "oppositeDirection" : true, "depth" : 89 * mm, "offsetDistance" : 25 * mm});
        }
    });
